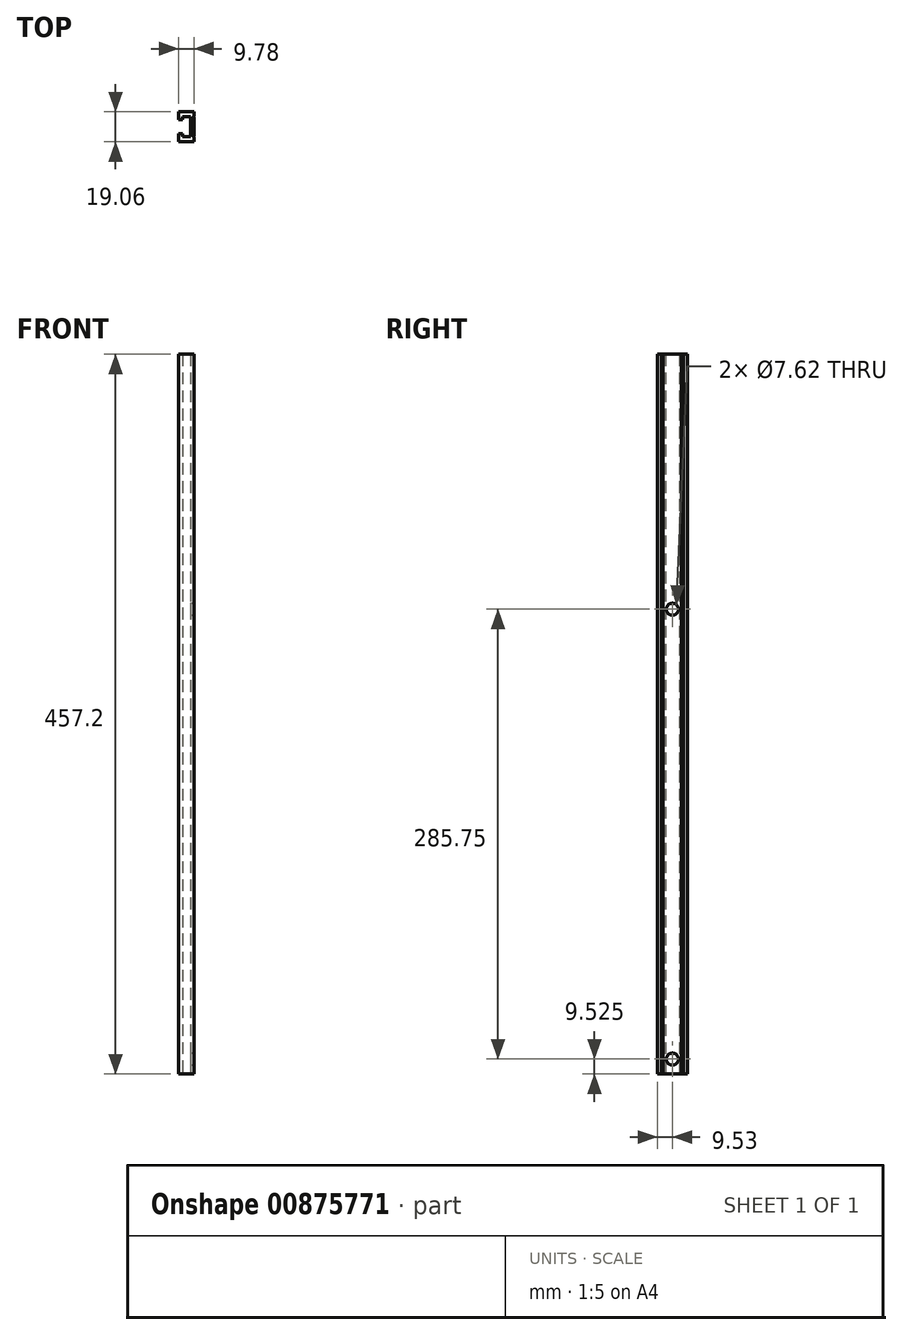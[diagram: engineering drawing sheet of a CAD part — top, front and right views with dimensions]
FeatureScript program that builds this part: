
annotation { "Feature Type Name" : "Feature", "Feature Type Description" : "" }
export const myFeature = defineFeature(function(context is Context, id is Id, definition is map)
    precondition{}
    {
        {
            var Q0;
            Q0=qCreatedBy(makeId("Top.planeOp"),FACE);
            var sketch = newSketch(context, id + "F0", { "sketchPlane" : qUnion([Q0])});
            skLineSegment(sketch, "E0.bottom", {"start": v(4.89, -9.52) * mm, "end": v(-4.89, -9.53) * mm});
            skLineSegment(sketch, "E0.top", {"start": v(4.89, 9.53) * mm, "end": v(-4.89, 9.53) * mm});
            skLineSegment(sketch, "E0.left", {"start": v(4.89, -9.52) * mm, "end": v(4.89, -6.86) * mm});
            skLineSegment(sketch, "E0.right", {"start": v(-4.89, -9.53) * mm, "end": v(-4.89, -4.45) * mm});
            skPoint(sketch, "E0.middle", {"position": v(0, 0) * mm});
            skLineSegment(sketch, "E1.bottom", {"start": v(-2.54, -4.45) * mm, "end": v(-4.89, -4.45) * mm});
            skLineSegment(sketch, "E1.top", {"start": v(-2.54, 4.45) * mm, "end": v(-4.89, 4.45) * mm});
            skPoint(sketch, "E1.middle", {"position": v(-4.89, 0) * mm});
            skLineSegment(sketch, "E2.bottom", {"start": v(2.54, -6.35) * mm, "end": v(-2.54, -6.35) * mm});
            skLineSegment(sketch, "E2.top", {"start": v(2.54, 6.35) * mm, "end": v(-2.54, 6.35) * mm});
            skLineSegment(sketch, "E2.left", {"start": v(2.54, -6.35) * mm, "end": v(2.54, 6.35) * mm});
            skLineSegment(sketch, "E2.right", {"start": v(-2.54, -6.35) * mm, "end": v(-2.54, -4.45) * mm});
            skLineSegment(sketch, "E3.trimOffspring", {"start": v(-4.89, 4.45) * mm, "end": v(-4.89, 9.53) * mm});
            skLineSegment(sketch, "E4.trimOffspring", {"start": v(-2.54, 4.45) * mm, "end": v(-2.54, 6.35) * mm});
            skPoint(sketch, "E5.orphan", {"position": v(-1.71, -4.45) * mm});
            skPoint(sketch, "E6.orphan", {"position": v(-1.71, 4.45) * mm});
            skPoint(sketch, "E7.orphan", {"position": v(-8.06, 4.45) * mm});
            skPoint(sketch, "E8.orphan", {"position": v(-8.06, -4.44) * mm});
            skArc(sketch, "E9", {"start": v(4.89, -5.87) * mm, "mid": v(4.6, -6.37) * mm, "end": v(4.89, -6.86) * mm});
            skArc(sketch, "E10.MirrorCS", {"start": v(4.89, 5.87) * mm, "mid": v(4.6, 6.37) * mm, "end": v(4.89, 6.86) * mm});
            skLineSegment(sketch, "E11.trimOffspring", {"start": v(4.89, 6.86) * mm, "end": v(4.89, 9.53) * mm});
            skLineSegment(sketch, "E12.trimOffspring", {"start": v(4.89, -5.87) * mm, "end": v(4.89, 5.87) * mm});
            skSolve(sketch);
        }
        {
            var Q0;
            Q0=qSketchRegion(id+"F0",true);
            extrude(context, id + "F1", {"entities" : qUnion([Q0]), "depth" : 457.2 * mm, "offsetDistance" : 25.4 * mm});
        }
        {
            var Q0;
            Q0=makeQuery(id+"F1.opExtrude","SWEPT_FACE",FACE,{"disambiguationData":[OSD([sQuery(id+"F0.wireOp",EDGE,"E12.trimOffspring")])]});
            var sketch = newSketch(context, id + "F2", { "sketchPlane" : qUnion([Q0])});
            skPoint(sketch, "E13", {"position": v(0, 447.68) * mm});
            skPoint(sketch, "E13.positionSnap0", {"position": v(0, 457.2) * mm});
            skPoint(sketch, "E14", {"position": v(0, 295.28) * mm});
            skPoint(sketch, "E15", {"position": v(0, 9.53) * mm});
            skSolve(sketch);
        }
        {
            var Q0;
            Q0=sQuery(id+"F2.wireOp",VERTEX,"E15");
            var Q1;
            Q1=sQuery(id+"F2.wireOp",VERTEX,"E14");
            var Q2;
            Q2=makeQuery(id+"F1.opExtrude","SWEPT_BODY",BODY,{"disambiguationData":[OSD([sQuery(id+"F0.wireOp",EDGE,"E0.bottom"),sQuery(id+"F0.wireOp",EDGE,"E0.top"),sQuery(id+"F0.wireOp",EDGE,"E0.left"),sQuery(id+"F0.wireOp",EDGE,"E0.right"),sQuery(id+"F0.wireOp",EDGE,"E1.bottom"),sQuery(id+"F0.wireOp",EDGE,"E1.top"),sQuery(id+"F0.wireOp",EDGE,"E2.bottom"),sQuery(id+"F0.wireOp",EDGE,"E2.top"),sQuery(id+"F0.wireOp",EDGE,"E2.left"),sQuery(id+"F0.wireOp",EDGE,"E2.right"),sQuery(id+"F0.wireOp",EDGE,"E3.trimOffspring"),sQuery(id+"F0.wireOp",EDGE,"E4.trimOffspring"),sQuery(id+"F0.wireOp",EDGE,"E9"),sQuery(id+"F0.wireOp",EDGE,"E10.MirrorCS"),sQuery(id+"F0.wireOp",EDGE,"E11.trimOffspring"),sQuery(id+"F0.wireOp",EDGE,"E12.trimOffspring")])]});
            hole(context, id + "F3", {"style" : HoleStyle.SIMPLE, "endStyle" : HoleEndStyle.BLIND, "holeDiameter" : 7.62 * mm, "majorDiameter" : 6.35 * mm, "holeDepth" : 25.4 * mm, "tappedDepth" : 76.2 * mm, "tapClearance" : 3, "startFromSketch" : true, "locations" : qUnion([Q0, Q1]), "scope" : qUnion([Q2])});
        }
    });
